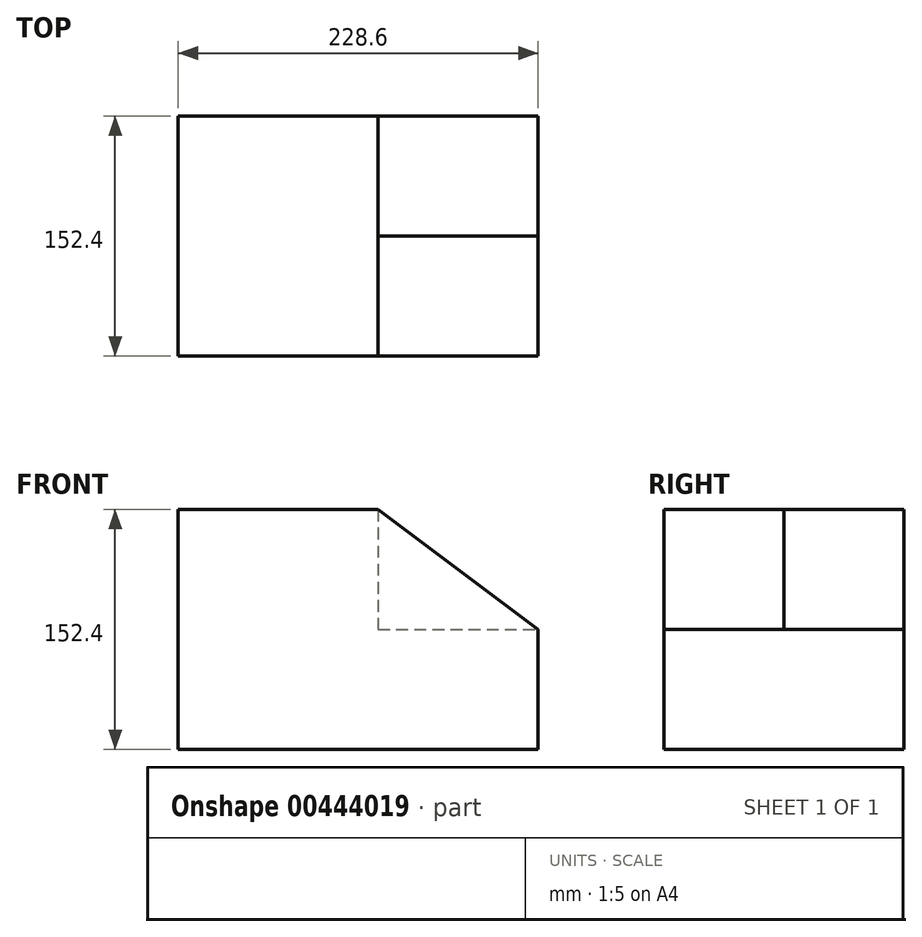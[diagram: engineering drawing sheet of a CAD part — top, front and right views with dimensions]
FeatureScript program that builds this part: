
annotation { "Feature Type Name" : "Feature", "Feature Type Description" : "" }
export const myFeature = defineFeature(function(context is Context, id is Id, definition is map)
    precondition{}
    {
        {
            var Q0;
            Q0=qCreatedBy(makeId("Front.planeOp"),FACE);
            var sketch = newSketch(context, id + "F0", { "sketchPlane" : qUnion([Q0])});
            skLineSegment(sketch, "E0", {"start": v(0, 0) * mm, "end": v(-228.6, 0) * mm});
            skLineSegment(sketch, "E1", {"start": v(-228.6, 0) * mm, "end": v(-228.6, 152.4) * mm});
            skLineSegment(sketch, "E2", {"start": v(-228.6, 152.4) * mm, "end": v(-101.6, 152.4) * mm});
            skLineSegment(sketch, "E3", {"start": v(-101.6, 152.4) * mm, "end": v(0, 76.2) * mm});
            skLineSegment(sketch, "E4", {"start": v(0, 76.2) * mm, "end": v(0, 0) * mm});
            skSolve(sketch);
        }
        {
            var Q0;
            Q0=makeQuery(id+"F0.imprint","IMPRINT",FACE,{"disambiguationData":[TD([[makeQuery(id+"F0.imprint","IMPRINT",EDGE,{"derivedFrom":sQuery(id+"F0.wireOp",EDGE,"E0")}),-1.0]])]});
            extrude(context, id + "F1", {"entities" : qUnion([Q0]), "endBound" : BoundingType.SYMMETRIC, "depth" : 152.4 * mm});
        }
        {
            var Q0;
            Q0=makeQuery(id+"F1.opExtrude","CAP_FACE",FACE,{"disambiguationData":[OSD([sQuery(id+"F0.wireOp",EDGE,"E0"),sQuery(id+"F0.wireOp",EDGE,"E1"),sQuery(id+"F0.wireOp",EDGE,"E2"),sQuery(id+"F0.wireOp",EDGE,"E3"),sQuery(id+"F0.wireOp",EDGE,"E4")])],"isStart":true});
            var sketch = newSketch(context, id + "F2", { "sketchPlane" : qUnion([Q0])});
            skLineSegment(sketch, "E5", {"start": v(101.6, 152.4) * mm, "end": v(101.6, 76.2) * mm});
            skLineSegment(sketch, "E6", {"start": v(101.6, 76.2) * mm, "end": v(0, 76.2) * mm});
            skSolve(sketch);
        }
        {
            var Q0;
            Q0=makeQuery(id+"F2.imprint","IMPRINT",FACE,{"disambiguationData":[TD([[makeQuery(id+"F2.imprint","IMPRINT",EDGE,{"derivedFrom":sQuery(id+"F2.wireOp",EDGE,"E5")}),-1.0]])]});
            extrude(context, id + "F3", {"entities" : qUnion([Q0]), "operationType" : NewBodyOperationType.REMOVE, "oppositeDirection" : true, "depth" : 76.2 * mm});
        }
    });
